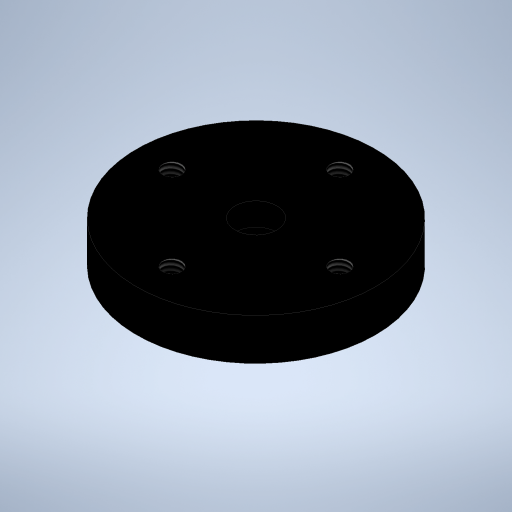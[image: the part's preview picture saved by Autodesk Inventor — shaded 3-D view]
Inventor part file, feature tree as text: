
AUTODESK INVENTOR PART (.ipt)
format: ipt  version: 2024.1 (Build 281209000, 209)  size: 273,920 bytes
history: native  units: mm
features: sketch x2, other x1, revolve x1, hole x1
ambient origin geometry x8: Origin, YZ Plane, XZ Plane, XY Plane, X Axis, Y Axis, Z Axis, Center Point
bodies: Body1 (feature_tree)
feature tree (5):
  other  "솔리드1"
  revolve  "회전1"
  hole  "Hole2"  [1 undecoded]
  sketch  "스케치1"
  sketch  "Sketch3"  dims[d1=1.75mm d2=2.925mm d4=3.48mm d6=4.5mm d7=9.96mm d8=1.9mm d9=90.0deg d22=5.5mm d23=7.0mm d24=40.0mm d26=360.0deg d28=1.567mm d29=3.48mm d30=4.0mm d31=2.0mm d32=90.0deg d33=5.0mm d34=0.0mm]
note: 1 required parameter value undecoded (feature->parameter linkage not recoverable at this tier; creation-order binding heuristic only, values carry confidence <= 0.55)
